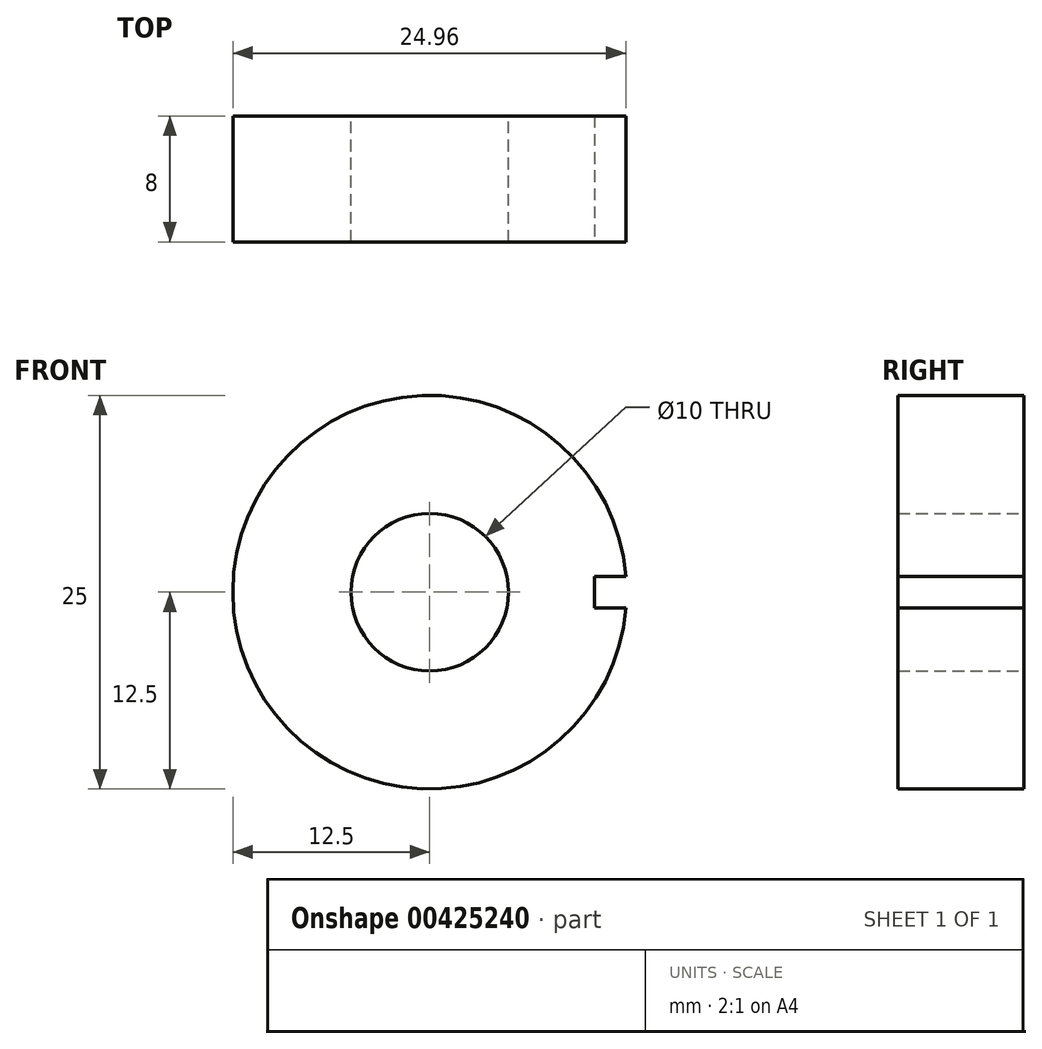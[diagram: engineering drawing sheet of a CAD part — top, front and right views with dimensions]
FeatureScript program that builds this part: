
annotation { "Feature Type Name" : "Feature", "Feature Type Description" : "" }
export const myFeature = defineFeature(function(context is Context, id is Id, definition is map)
    precondition{}
    {
        {
            var Q0;
            Q0=qCreatedBy(makeId("Front.planeOp"),FACE);
            var sketch = newSketch(context, id + "F0", { "sketchPlane" : qUnion([Q0])});
            skCircle(sketch, "E0", {"center": v(0, 0) * mm, "radius": 12.5 * mm});
            skCircle(sketch, "E1", {"center": v(0, 0) * mm, "radius": 5 * mm});
            skSolve(sketch);
        }
        {
            var Q0;
            Q0=makeQuery(id+"F0.imprint","IMPRINT",FACE,{"disambiguationData":[TD([[makeQuery(id+"F0.imprint","IMPRINT",EDGE,{"derivedFrom":sQuery(id+"F0.wireOp",EDGE,"E0")}),1.0]])]});
            extrude(context, id + "F1", {"entities" : qUnion([Q0]), "endBound" : BoundingType.SYMMETRIC, "depth" : 8 * mm});
        }
        {
            var Q0;
            Q0=makeQuery(id+"F1.opExtrude","CAP_FACE",FACE,{"disambiguationData":[OSD([sQuery(id+"F0.wireOp",EDGE,"E0"),sQuery(id+"F0.wireOp",EDGE,"E1")])],"isStart":false});
            var sketch = newSketch(context, id + "F2", { "sketchPlane" : qUnion([Q0])});
            skLineSegment(sketch, "E2.0", {"start": v(10.45, -1) * mm, "end": v(12.46, -1) * mm});
            skLineSegment(sketch, "E3.MirrorCS", {"start": v(10.45, 1) * mm, "end": v(12.46, 1) * mm});
            skLineSegment(sketch, "E4", {"start": v(10.45, -1) * mm, "end": v(10.45, 1) * mm});
            skPoint(sketch, "E5.orphan", {"position": v(0, 1) * mm});
            skPoint(sketch, "E6.orphan", {"position": v(0, -1) * mm});
            skSolve(sketch);
        }
        {
            var Q0;
            {var subQ0=sQuery(id+"F2.wireOp",EDGE,"E2.0");Q0=makeQuery(id+"F2.imprint","IMPRINT",FACE,{"disambiguationData":[TD([[makeQuery(id+"F2.imprint","IMPRINT",EDGE,{"derivedFrom":subQ0}),1.0]])]});}
            extrude(context, id + "F3", {"entities" : qUnion([Q0]), "operationType" : NewBodyOperationType.REMOVE, "oppositeDirection" : true, "depth" : 25 * mm});
        }
    });
